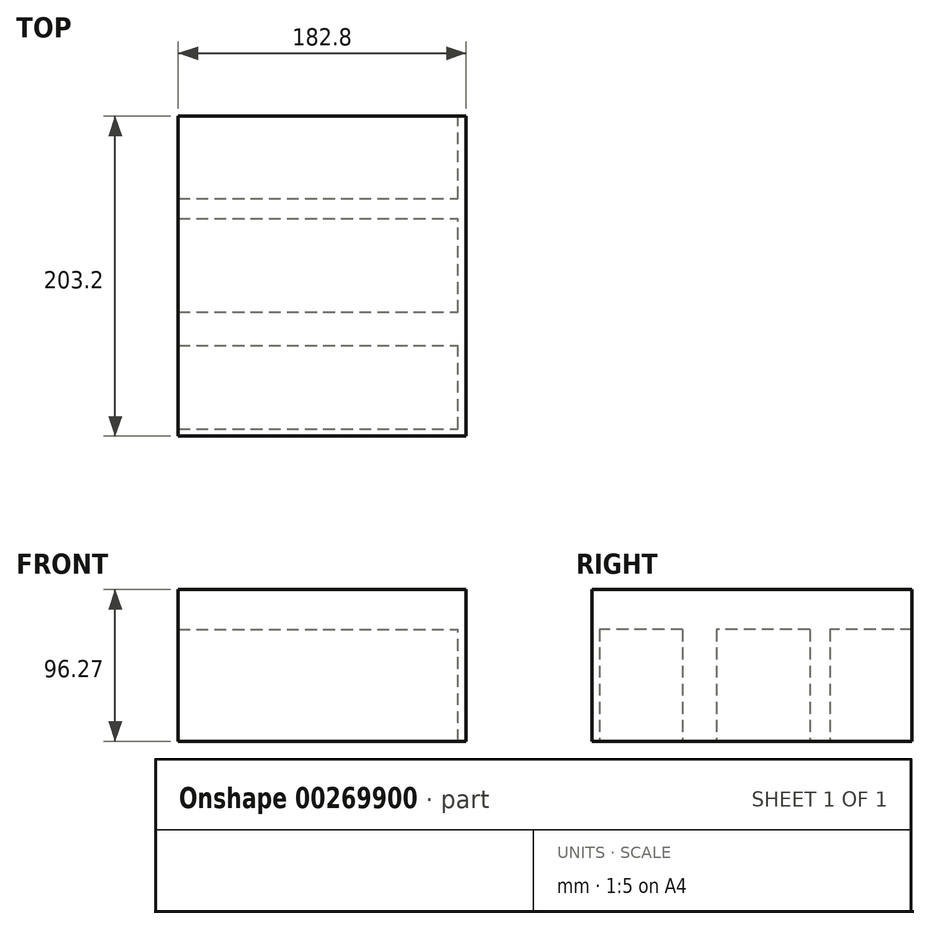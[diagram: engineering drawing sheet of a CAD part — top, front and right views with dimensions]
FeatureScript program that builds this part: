
annotation { "Feature Type Name" : "Feature", "Feature Type Description" : "" }
export const myFeature = defineFeature(function(context is Context, id is Id, definition is map)
    precondition{}
    {
        {
            var Q0;
            Q0=qCreatedBy(makeId("Top.planeOp"),FACE);
            var sketch = newSketch(context, id + "F0", { "sketchPlane" : qUnion([Q0])});
            skLineSegment(sketch, "E0.bottom", {"start": v(-88.9, 137.87) * mm, "end": v(88.9, 137.87) * mm});
            skLineSegment(sketch, "E0.top", {"start": v(-88.9, -65.33) * mm, "end": v(88.9, -65.33) * mm});
            skLineSegment(sketch, "E0.left", {"start": v(-88.9, 137.87) * mm, "end": v(-88.9, -65.33) * mm});
            skLineSegment(sketch, "E0.right", {"start": v(88.9, 137.87) * mm, "end": v(88.9, -65.33) * mm});
            skLineSegment(sketch, "E1.top", {"start": v(-88.9, 85.67) * mm, "end": v(88.9, 85.67) * mm});
            skLineSegment(sketch, "E1.left", {"start": v(-88.9, 137.87) * mm, "end": v(-88.9, 85.67) * mm});
            skLineSegment(sketch, "E1.right", {"start": v(88.9, 137.87) * mm, "end": v(88.9, 85.67) * mm});
            skLineSegment(sketch, "E2.bottom", {"start": v(-88.9, 73) * mm, "end": v(88.9, 73) * mm});
            skLineSegment(sketch, "E2.top", {"start": v(-88.9, 13.58) * mm, "end": v(88.9, 13.58) * mm});
            skLineSegment(sketch, "E2.left", {"start": v(-88.9, 73) * mm, "end": v(-88.9, 13.58) * mm});
            skLineSegment(sketch, "E2.right", {"start": v(88.9, 73) * mm, "end": v(88.9, 13.58) * mm});
            skLineSegment(sketch, "E3.bottom", {"start": v(-88.9, -7.83) * mm, "end": v(88.9, -7.83) * mm});
            skLineSegment(sketch, "E3.top", {"start": v(-88.9, -60.7) * mm, "end": v(88.9, -60.7) * mm});
            skLineSegment(sketch, "E3.left", {"start": v(-88.9, -7.83) * mm, "end": v(-88.9, -60.7) * mm});
            skLineSegment(sketch, "E3.right", {"start": v(88.9, -7.83) * mm, "end": v(88.9, -60.7) * mm});
            skSolve(sketch);
        }
        {
            var Q0;
            {var subQ0=sQuery(id+"F0.wireOp",EDGE,"E2.top");Q0=makeQuery(id+"F0.imprint","IMPRINT",FACE,{"disambiguationData":[TD([[makeQuery(id+"F0.imprint","IMPRINT",EDGE,{"derivedFrom":subQ0}),-1.0]])]});}
            var Q1;
            Q1=makeQuery(id+"F0.imprint","IMPRINT",FACE,{"disambiguationData":[TD([[makeQuery(id+"F0.imprint","IMPRINT",EDGE,{"derivedFrom":sQuery(id+"F0.wireOp",EDGE,"E2.bottom")}),-1.0]])]});
            var Q2;
            Q2=makeQuery(id+"F0.imprint","IMPRINT",FACE,{"disambiguationData":[TD([[makeQuery(id+"F0.imprint","IMPRINT",EDGE,{"derivedFrom":sQuery(id+"F0.wireOp",EDGE,"E0.bottom")}),-1.0]])]});
            var Q3;
            {var subQ0=sQuery(id+"F0.wireOp",EDGE,"E1.top");Q3=makeQuery(id+"F0.imprint","IMPRINT",FACE,{"disambiguationData":[TD([[makeQuery(id+"F0.imprint","IMPRINT",EDGE,{"derivedFrom":subQ0}),-1.0]])]});}
            var Q4;
            Q4=makeQuery(id+"F0.imprint","IMPRINT",FACE,{"disambiguationData":[TD([[makeQuery(id+"F0.imprint","IMPRINT",EDGE,{"derivedFrom":sQuery(id+"F0.wireOp",EDGE,"E3.bottom")}),-1.0]])]});
            var Q5;
            {var subQ0=sQuery(id+"F0.wireOp",EDGE,"E0.top");Q5=makeQuery(id+"F0.imprint","IMPRINT",FACE,{"disambiguationData":[TD([[makeQuery(id+"F0.imprint","IMPRINT",EDGE,{"derivedFrom":subQ0}),1.0]])]});}
            extrude(context, id + "F1", {"entities" : qUnion([Q0, Q1, Q2, Q3, Q4, Q5]), "depth" : 70.87 * mm});
        }
        {
            var Q0;
            Q0=makeQuery(id+"F1.opExtrude","CAP_FACE",FACE,{"disambiguationData":[OSD([sQuery(id+"F0.wireOp",EDGE,"E0.top"),sQuery(id+"F0.wireOp",EDGE,"E0.left"),sQuery(id+"F0.wireOp",EDGE,"E0.right"),sQuery(id+"F0.wireOp",EDGE,"E0.bottom"),sQuery(id+"F0.wireOp",EDGE,"E1.left"),sQuery(id+"F0.wireOp",EDGE,"E1.right"),sQuery(id+"F0.wireOp",EDGE,"E2.left"),sQuery(id+"F0.wireOp",EDGE,"E2.right"),sQuery(id+"F0.wireOp",EDGE,"E3.left"),sQuery(id+"F0.wireOp",EDGE,"E3.right")])],"isStart":false});
            extrude(context, id + "F2", {"entities" : qUnion([Q0]), "operationType" : NewBodyOperationType.ADD, "depth" : 25.4 * mm});
        }
        {
            var Q0;
            Q0=makeQuery(id+"F0.imprint","IMPRINT",FACE,{"disambiguationData":[TD([[makeQuery(id+"F0.imprint","IMPRINT",EDGE,{"derivedFrom":sQuery(id+"F0.wireOp",EDGE,"E3.bottom")}),-1.0]])]});
            var Q1;
            Q1=makeQuery(id+"F0.imprint","IMPRINT",FACE,{"disambiguationData":[TD([[makeQuery(id+"F0.imprint","IMPRINT",EDGE,{"derivedFrom":sQuery(id+"F0.wireOp",EDGE,"E2.bottom")}),-1.0]])]});
            var Q2;
            Q2=makeQuery(id+"F0.imprint","IMPRINT",FACE,{"disambiguationData":[TD([[makeQuery(id+"F0.imprint","IMPRINT",EDGE,{"derivedFrom":sQuery(id+"F0.wireOp",EDGE,"E0.bottom")}),-1.0]])]});
            extrude(context, id + "F3", {"entities" : qUnion([Q0, Q1, Q2]), "operationType" : NewBodyOperationType.REMOVE, "depth" : 71 * mm});
        }
        {
            var Q0;
            {var subQ0=sQuery(id+"F0.wireOp",EDGE,"E3.right");var subQ1=sQuery(id+"F0.wireOp",EDGE,"E2.right");var subQ2=sQuery(id+"F0.wireOp",EDGE,"E1.right");var subQ3=sQuery(id+"F0.wireOp",EDGE,"E0.right");Q0=makeQuery(id+"F2.boolean.opBoolean","MERGE",FACE,{"derivedFrom":[makeQuery(id+"F1.opExtrude","SWEPT_FACE",FACE,{"disambiguationData":[OSD([subQ3,subQ2,subQ1,subQ0])]}),makeQuery(id+"F2.opExtrude","SWEPT_FACE",FACE,{"disambiguationData":[OSD([subQ3,subQ2,subQ1,subQ0])]})]});}
            var sketch = newSketch(context, id + "F4", { "sketchPlane" : qUnion([Q0])});
            skLineSegment(sketch, "E4.bottom", {"start": v(-65.33, 0) * mm, "end": v(137.87, 0) * mm});
            skLineSegment(sketch, "E4.top", {"start": v(-65.33, 96.27) * mm, "end": v(137.87, 96.27) * mm});
            skLineSegment(sketch, "E4.left", {"start": v(-65.33, 0) * mm, "end": v(-65.33, 96.27) * mm});
            skLineSegment(sketch, "E4.right", {"start": v(137.87, 0) * mm, "end": v(137.87, 96.27) * mm});
            skSolve(sketch);
        }
        {
            var Q0;
            Q0 = qSketchRegion(id + "F4", true);
            extrude(context, id + "F5", {"entities" : qUnion([Q0]), "operationType" : NewBodyOperationType.ADD, "depth" : 5 * mm});
        }
    });
